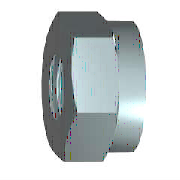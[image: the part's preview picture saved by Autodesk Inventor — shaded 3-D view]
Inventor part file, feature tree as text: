
AUTODESK INVENTOR PART (.ipt)
format: ipt  version: 2022 (Build 260153000, 153)  size: 179,712 bytes
history: native  units: mm (DEFAULTED — no unit token found)
features: sketch x4, extrude x1, chamfer x1, hole x1, other x1, plane x1
ambient origin geometry x7: Origin, YZ Plane, XZ Plane, X Axis, Y Axis, Z Axis, Center Point
bodies: Solid1 (feature_tree), Body (feature_tree)
feature tree (9):
  extrude  "Ring"  Depth=4.125mm
  chamfer  "Chamfer1"  Distance=8.88mm
  hole  "Thread"  [1 undecoded]
  other  "Work Axis1"
  plane  "Work Plane1"
  sketch  "Sketch1"  dims[d0=11.547005mm d1=4.125mm]
  sketch  "Sketch3"  dims[d3=30.0deg]
  sketch  "Sketch2"  dims[d2=0.0mm]
  sketch  "Sketch4"  dims[d4=30.0deg d5=8.88mm d6=8.88mm d26=90.0deg d7=8.88mm d8=1.875mm d9=0.0mm d30=4.917mm d31=6.0mm d32=4.0mm d33=2.0mm d34=14.3117mm d35=8.0mm d36=20.594885mm d10=0.541266mm d11=30.0deg d12=0.541266mm d13=30.0deg d14=0.0mm d15=0.0mm d45=0.0mm d46=0.541266mm d47=0.541266mm d48=0.0mm]
note: 1 required parameter value undecoded (feature->parameter linkage not recoverable at this tier; creation-order binding heuristic only, values carry confidence <= 0.55)
